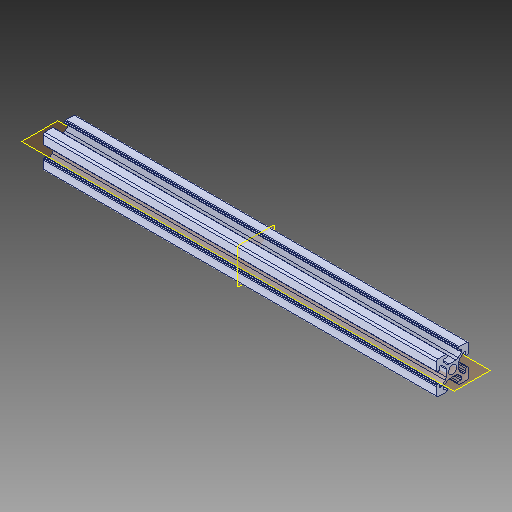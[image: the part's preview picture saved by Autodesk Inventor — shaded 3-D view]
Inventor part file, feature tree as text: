
AUTODESK INVENTOR PART (.ipt)
format: ipt  version: 2018 (Build 220112000, 112)  size: 380,928 bytes
history: native  units: in
note: dims shown in document units (in); Inventor stores cm internally (conversion verified against a paired STEP export)
features: extrude x1, plane x1, sketch x1, projected_geometry x1, fillet x1
ambient origin geometry x8: Origin, YZ Plane, XZ Plane, XY Plane, X Axis, Y Axis, Z Axis, Center Point
bodies: Solid1 (feature_tree)
feature tree (5):
  extrude  "Extrusion2"  [1 undecoded]
  plane  "Work Plane1"
  sketch  "Sketch3"  dims[d2=5.5118in d3=0.0in]
  projected_geometry  "Projected Loop2"
  fillet  "Fillet5"  [1 undecoded]
note: 2 required parameter values undecoded (feature->parameter linkage not recoverable at this tier; creation-order binding heuristic only, values carry confidence <= 0.55)
